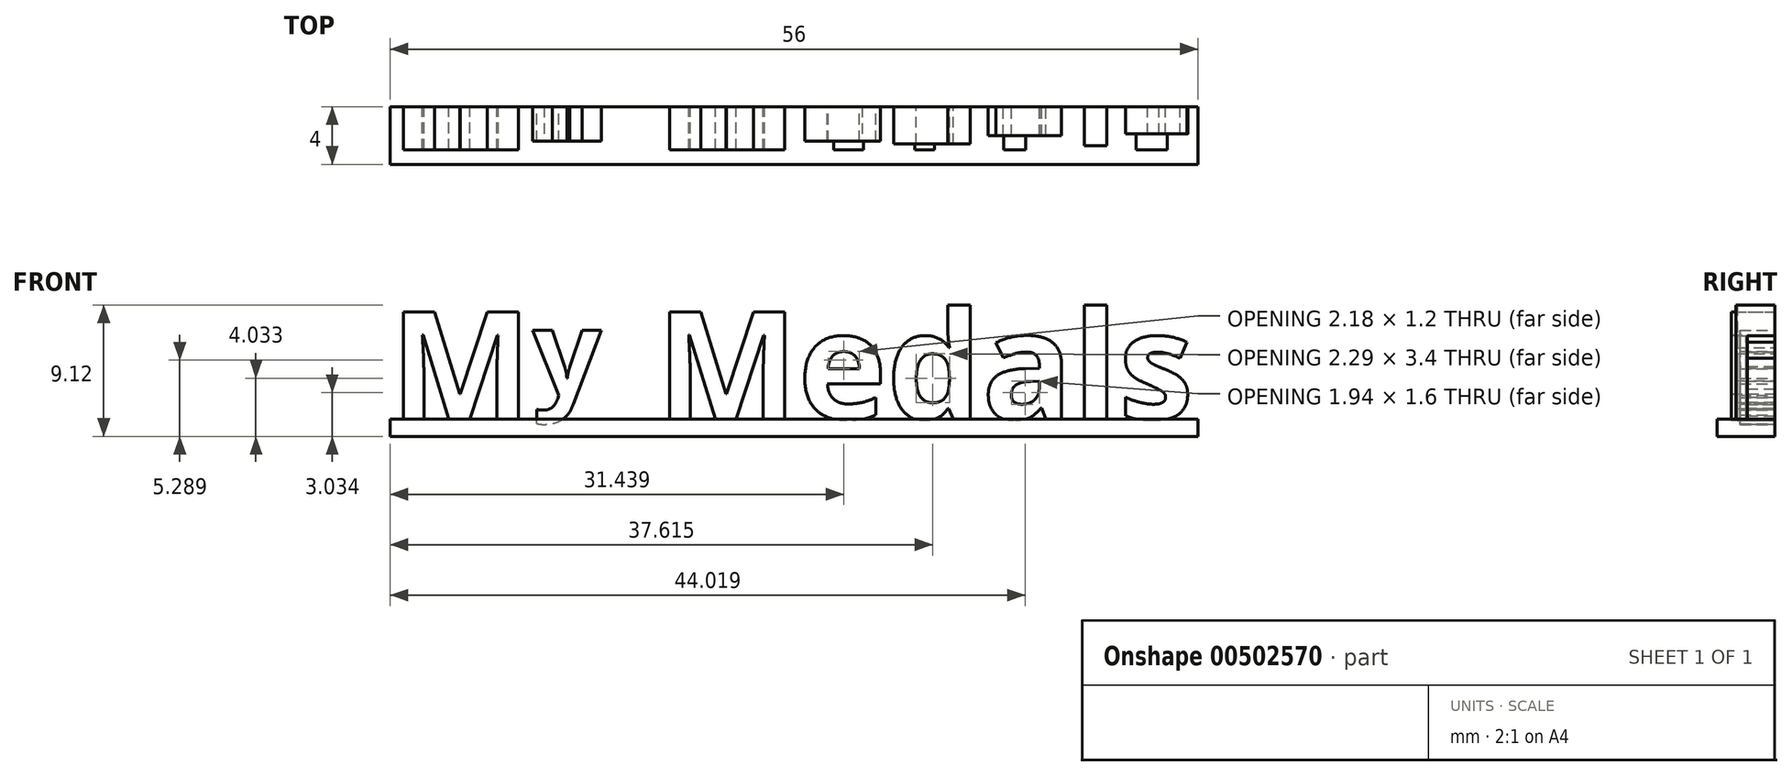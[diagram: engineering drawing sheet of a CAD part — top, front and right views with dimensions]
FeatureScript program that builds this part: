
annotation { "Feature Type Name" : "Feature", "Feature Type Description" : "" }
export const myFeature = defineFeature(function(context is Context, id is Id, definition is map)
    precondition{}
    {
        {
            var Q0;
            Q0=qCreatedBy(makeId("Front.planeOp"),FACE);
            var sketch = newSketch(context, id + "F0", { "sketchPlane" : qUnion([Q0])});
            skText(sketch, "E0", { "text": "My Medals", "fontName": "NotoSans-Bold.ttf"});
            const initialGuessF0  = {"E0": [0, 0, 1, 0, 0.0075]};
            skSetInitialGuess(sketch, initialGuessF0);
            skSolve(sketch);
        }
        {
            var Q0;
            Q0 = qSketchRegion(id + "F0", true);
            extrude(context, id + "F1", {"entities" : qUnion([Q0]), "depth" : 3 * mm, "offsetDistance" : 25 * mm});
        }
        {
            var Q0;
            Q0=makeQuery(id+"F1.opExtrude","SWEPT_BODY",BODY,{"disambiguationData":[OSD([sQuery(id+"F0.wireOp",EDGE,"E0.sketch_text.stroke-19"),sQuery(id+"F0.wireOp",EDGE,"E0.sketch_text.stroke-20"),sQuery(id+"F0.wireOp",EDGE,"E0.sketch_text.stroke-21"),sQuery(id+"F0.wireOp",EDGE,"E0.sketch_text.stroke-22"),sQuery(id+"F0.wireOp",EDGE,"E0.sketch_text.stroke-23"),sQuery(id+"F0.wireOp",EDGE,"E0.sketch_text.stroke-24"),sQuery(id+"F0.wireOp",EDGE,"E0.sketch_text.stroke-25"),sQuery(id+"F0.wireOp",EDGE,"E0.sketch_text.stroke-26"),sQuery(id+"F0.wireOp",EDGE,"E0.sketch_text.stroke-27"),sQuery(id+"F0.wireOp",EDGE,"E0.sketch_text.stroke-28"),sQuery(id+"F0.wireOp",EDGE,"E0.sketch_text.stroke-29"),sQuery(id+"F0.wireOp",EDGE,"E0.sketch_text.stroke-30"),sQuery(id+"F0.wireOp",EDGE,"E0.sketch_text.stroke-31"),sQuery(id+"F0.wireOp",EDGE,"E0.sketch_text.stroke-32"),sQuery(id+"F0.wireOp",EDGE,"E0.sketch_text.stroke-33"),sQuery(id+"F0.wireOp",EDGE,"E0.sketch_text.stroke-34"),sQuery(id+"F0.wireOp",EDGE,"E0.sketch_text.stroke-35")])]});
            transform(context, id + "F2", {"entities" : qUnion([Q0]), "transformType" : TransformType.TRANSLATION_3D, "dx" : 0 * mm, "dy" : 0 * mm, "dz" : 1.86 * mm, "makeCopy" : false});
        }
        {
            var Q0;
            Q0=qCreatedBy(makeId("Front.planeOp"),FACE);
            var sketch = newSketch(context, id + "F3", { "sketchPlane" : qUnion([Q0])});
            skLineSegment(sketch, "E1.bottom", {"start": v(19.37, -15.05) * mm, "end": v(75.37, -15.05) * mm});
            skLineSegment(sketch, "E1.top", {"start": v(19.37, -16.25) * mm, "end": v(75.37, -16.25) * mm});
            skLineSegment(sketch, "E1.left", {"start": v(19.37, -15.05) * mm, "end": v(19.37, -16.25) * mm});
            skLineSegment(sketch, "E1.right", {"start": v(75.37, -15.05) * mm, "end": v(75.37, -16.25) * mm});
            skSolve(sketch);
        }
        {
            var Q0;
            Q0=makeQuery(id+"F3.imprint","IMPRINT",FACE,{"disambiguationData":[TD([[makeQuery(id+"F3.imprint","IMPRINT",EDGE,{"derivedFrom":sQuery(id+"F3.wireOp",EDGE,"E1.bottom")}),-1.0]])]});
            extrude(context, id + "F4", {"entities" : qUnion([Q0]), "depth" : 4 * mm, "offsetDistance" : 25 * mm});
        }
        {
            var Q0;
            Q0=makeQuery(id+"F4.opExtrude","SWEPT_BODY",BODY,{"disambiguationData":[OSD([sQuery(id+"F3.wireOp",EDGE,"E1.bottom"),sQuery(id+"F3.wireOp",EDGE,"E1.top"),sQuery(id+"F3.wireOp",EDGE,"E1.left"),sQuery(id+"F3.wireOp",EDGE,"E1.right")])]});
            var Q1;
            Q1=makeQuery(id+"F4.opExtrude","CAP_VERTEX",VERTEX,{"disambiguationData":[OSD([sQuery(id+"F3.wireOp",EDGE,"E1.bottom"),sQuery(id+"F3.wireOp",EDGE,"E1.left")])],"isStart":true});
            var Q2;
            Q2=qCreatedBy(makeId("Origin.pointOp"),VERTEX);
            transform(context, id + "F5", {"entities" : qUnion([Q0]), "transformType" : TransformType.TRANSLATION_ENTITY, "oppositeDirectionEntity" : false, "transformLine" : qUnion([Q1, Q2]), "makeCopy" : false});
        }
        {
            var Q0;
            Q0=makeQuery(id+"F1.opExtrude","SWEPT_BODY",BODY,{"disambiguationData":[OSD([sQuery(id+"F0.wireOp",EDGE,"E0.sketch_text.stroke-19"),sQuery(id+"F0.wireOp",EDGE,"E0.sketch_text.stroke-20"),sQuery(id+"F0.wireOp",EDGE,"E0.sketch_text.stroke-21"),sQuery(id+"F0.wireOp",EDGE,"E0.sketch_text.stroke-22"),sQuery(id+"F0.wireOp",EDGE,"E0.sketch_text.stroke-23"),sQuery(id+"F0.wireOp",EDGE,"E0.sketch_text.stroke-24"),sQuery(id+"F0.wireOp",EDGE,"E0.sketch_text.stroke-25"),sQuery(id+"F0.wireOp",EDGE,"E0.sketch_text.stroke-26"),sQuery(id+"F0.wireOp",EDGE,"E0.sketch_text.stroke-27"),sQuery(id+"F0.wireOp",EDGE,"E0.sketch_text.stroke-28"),sQuery(id+"F0.wireOp",EDGE,"E0.sketch_text.stroke-29"),sQuery(id+"F0.wireOp",EDGE,"E0.sketch_text.stroke-30"),sQuery(id+"F0.wireOp",EDGE,"E0.sketch_text.stroke-31"),sQuery(id+"F0.wireOp",EDGE,"E0.sketch_text.stroke-32"),sQuery(id+"F0.wireOp",EDGE,"E0.sketch_text.stroke-33"),sQuery(id+"F0.wireOp",EDGE,"E0.sketch_text.stroke-34"),sQuery(id+"F0.wireOp",EDGE,"E0.sketch_text.stroke-35")])]});
            var Q1;
            Q1=makeQuery(id+"F1.opExtrude","CAP_VERTEX",VERTEX,{"disambiguationData":[OSD([sQuery(id+"F0.wireOp",EDGE,"E0.sketch_text.stroke-30"),sQuery(id+"F0.wireOp",EDGE,"E0.sketch_text.stroke-31")])],"isStart":true});
            transform(context, id + "F6", {"entities" : qUnion([Q0]), "transformType" : TransformType.SCALE_UNIFORMLY, "scale" : .8, "scalePoint" : qUnion([Q1]), "makeCopy" : false});
        }
        {
            var Q0;
            Q0=makeQuery(id+"F1.opExtrude","CAP_FACE",FACE,{"disambiguationData":[OSD([sQuery(id+"F0.wireOp",EDGE,"E0.sketch_text.stroke-55"),sQuery(id+"F0.wireOp",EDGE,"E0.sketch_text.stroke-56"),sQuery(id+"F0.wireOp",EDGE,"E0.sketch_text.stroke-57"),sQuery(id+"F0.wireOp",EDGE,"E0.sketch_text.stroke-58"),sQuery(id+"F0.wireOp",EDGE,"E0.sketch_text.stroke-59"),sQuery(id+"F0.wireOp",EDGE,"E0.sketch_text.stroke-60"),sQuery(id+"F0.wireOp",EDGE,"E0.sketch_text.stroke-61"),sQuery(id+"F0.wireOp",EDGE,"E0.sketch_text.stroke-62"),sQuery(id+"F0.wireOp",EDGE,"E0.sketch_text.stroke-63"),sQuery(id+"F0.wireOp",EDGE,"E0.sketch_text.stroke-64"),sQuery(id+"F0.wireOp",EDGE,"E0.sketch_text.stroke-65"),sQuery(id+"F0.wireOp",EDGE,"E0.sketch_text.stroke-66"),sQuery(id+"F0.wireOp",EDGE,"E0.sketch_text.stroke-67"),sQuery(id+"F0.wireOp",EDGE,"E0.sketch_text.stroke-68"),sQuery(id+"F0.wireOp",EDGE,"E0.sketch_text.stroke-69"),sQuery(id+"F0.wireOp",EDGE,"E0.sketch_text.stroke-70"),sQuery(id+"F0.wireOp",EDGE,"E0.sketch_text.stroke-71"),sQuery(id+"F0.wireOp",EDGE,"E0.sketch_text.stroke-72"),sQuery(id+"F0.wireOp",EDGE,"E0.sketch_text.stroke-73"),sQuery(id+"F0.wireOp",EDGE,"E0.sketch_text.stroke-74")])],"isStart":false});
            extrude(context, id + "F7", {"entities" : qUnion([Q0]), "operationType" : NewBodyOperationType.REMOVE, "oppositeDirection" : true, "depth" : .6 * mm, "offsetDistance" : 25 * mm});
        }
        {
            var Q0;
            Q0=makeQuery(id+"F1.opExtrude","CAP_FACE",FACE,{"disambiguationData":[OSD([sQuery(id+"F0.wireOp",EDGE,"E0.sketch_text.stroke-75"),sQuery(id+"F0.wireOp",EDGE,"E0.sketch_text.stroke-76"),sQuery(id+"F0.wireOp",EDGE,"E0.sketch_text.stroke-77"),sQuery(id+"F0.wireOp",EDGE,"E0.sketch_text.stroke-78"),sQuery(id+"F0.wireOp",EDGE,"E0.sketch_text.stroke-79"),sQuery(id+"F0.wireOp",EDGE,"E0.sketch_text.stroke-80"),sQuery(id+"F0.wireOp",EDGE,"E0.sketch_text.stroke-81"),sQuery(id+"F0.wireOp",EDGE,"E0.sketch_text.stroke-82"),sQuery(id+"F0.wireOp",EDGE,"E0.sketch_text.stroke-83"),sQuery(id+"F0.wireOp",EDGE,"E0.sketch_text.stroke-84"),sQuery(id+"F0.wireOp",EDGE,"E0.sketch_text.stroke-85"),sQuery(id+"F0.wireOp",EDGE,"E0.sketch_text.stroke-86"),sQuery(id+"F0.wireOp",EDGE,"E0.sketch_text.stroke-87"),sQuery(id+"F0.wireOp",EDGE,"E0.sketch_text.stroke-88"),sQuery(id+"F0.wireOp",EDGE,"E0.sketch_text.stroke-89"),sQuery(id+"F0.wireOp",EDGE,"E0.sketch_text.stroke-90"),sQuery(id+"F0.wireOp",EDGE,"E0.sketch_text.stroke-91"),sQuery(id+"F0.wireOp",EDGE,"E0.sketch_text.stroke-92"),sQuery(id+"F0.wireOp",EDGE,"E0.sketch_text.stroke-93"),sQuery(id+"F0.wireOp",EDGE,"E0.sketch_text.stroke-94"),sQuery(id+"F0.wireOp",EDGE,"E0.sketch_text.stroke-95"),sQuery(id+"F0.wireOp",EDGE,"E0.sketch_text.stroke-96"),sQuery(id+"F0.wireOp",EDGE,"E0.sketch_text.stroke-97")])],"isStart":false});
            extrude(context, id + "F8", {"entities" : qUnion([Q0]), "operationType" : NewBodyOperationType.REMOVE, "oppositeDirection" : true, "depth" : .4 * mm, "offsetDistance" : 25 * mm});
        }
        {
            var Q0;
            Q0=makeQuery(id+"F1.opExtrude","CAP_FACE",FACE,{"disambiguationData":[OSD([sQuery(id+"F0.wireOp",EDGE,"E0.sketch_text.stroke-98"),sQuery(id+"F0.wireOp",EDGE,"E0.sketch_text.stroke-99"),sQuery(id+"F0.wireOp",EDGE,"E0.sketch_text.stroke-100"),sQuery(id+"F0.wireOp",EDGE,"E0.sketch_text.stroke-101"),sQuery(id+"F0.wireOp",EDGE,"E0.sketch_text.stroke-102"),sQuery(id+"F0.wireOp",EDGE,"E0.sketch_text.stroke-103"),sQuery(id+"F0.wireOp",EDGE,"E0.sketch_text.stroke-104"),sQuery(id+"F0.wireOp",EDGE,"E0.sketch_text.stroke-105"),sQuery(id+"F0.wireOp",EDGE,"E0.sketch_text.stroke-106"),sQuery(id+"F0.wireOp",EDGE,"E0.sketch_text.stroke-107"),sQuery(id+"F0.wireOp",EDGE,"E0.sketch_text.stroke-108"),sQuery(id+"F0.wireOp",EDGE,"E0.sketch_text.stroke-109"),sQuery(id+"F0.wireOp",EDGE,"E0.sketch_text.stroke-110"),sQuery(id+"F0.wireOp",EDGE,"E0.sketch_text.stroke-111"),sQuery(id+"F0.wireOp",EDGE,"E0.sketch_text.stroke-112"),sQuery(id+"F0.wireOp",EDGE,"E0.sketch_text.stroke-113"),sQuery(id+"F0.wireOp",EDGE,"E0.sketch_text.stroke-114"),sQuery(id+"F0.wireOp",EDGE,"E0.sketch_text.stroke-115"),sQuery(id+"F0.wireOp",EDGE,"E0.sketch_text.stroke-116"),sQuery(id+"F0.wireOp",EDGE,"E0.sketch_text.stroke-117"),sQuery(id+"F0.wireOp",EDGE,"E0.sketch_text.stroke-118"),sQuery(id+"F0.wireOp",EDGE,"E0.sketch_text.stroke-119"),sQuery(id+"F0.wireOp",EDGE,"E0.sketch_text.stroke-120"),sQuery(id+"F0.wireOp",EDGE,"E0.sketch_text.stroke-121"),sQuery(id+"F0.wireOp",EDGE,"E0.sketch_text.stroke-122")])],"isStart":false});
            extrude(context, id + "F9", {"entities" : qUnion([Q0]), "operationType" : NewBodyOperationType.REMOVE, "oppositeDirection" : true, "depth" : 1 * mm, "offsetDistance" : 25 * mm});
        }
        {
            var Q0;
            Q0=makeQuery(id+"F1.opExtrude","CAP_FACE",FACE,{"disambiguationData":[OSD([sQuery(id+"F0.wireOp",EDGE,"E0.sketch_text.stroke-123"),sQuery(id+"F0.wireOp",EDGE,"E0.sketch_text.stroke-124"),sQuery(id+"F0.wireOp",EDGE,"E0.sketch_text.stroke-125"),sQuery(id+"F0.wireOp",EDGE,"E0.sketch_text.stroke-126")])],"isStart":false});
            extrude(context, id + "F10", {"entities" : qUnion([Q0]), "operationType" : NewBodyOperationType.REMOVE, "oppositeDirection" : true, "depth" : .3 * mm, "offsetDistance" : 25 * mm});
        }
        {
            var Q0;
            Q0=makeQuery(id+"F1.opExtrude","CAP_FACE",FACE,{"disambiguationData":[OSD([sQuery(id+"F0.wireOp",EDGE,"E0.sketch_text.stroke-127"),sQuery(id+"F0.wireOp",EDGE,"E0.sketch_text.stroke-128"),sQuery(id+"F0.wireOp",EDGE,"E0.sketch_text.stroke-129"),sQuery(id+"F0.wireOp",EDGE,"E0.sketch_text.stroke-130"),sQuery(id+"F0.wireOp",EDGE,"E0.sketch_text.stroke-131"),sQuery(id+"F0.wireOp",EDGE,"E0.sketch_text.stroke-132"),sQuery(id+"F0.wireOp",EDGE,"E0.sketch_text.stroke-133"),sQuery(id+"F0.wireOp",EDGE,"E0.sketch_text.stroke-134"),sQuery(id+"F0.wireOp",EDGE,"E0.sketch_text.stroke-135"),sQuery(id+"F0.wireOp",EDGE,"E0.sketch_text.stroke-136"),sQuery(id+"F0.wireOp",EDGE,"E0.sketch_text.stroke-137"),sQuery(id+"F0.wireOp",EDGE,"E0.sketch_text.stroke-138"),sQuery(id+"F0.wireOp",EDGE,"E0.sketch_text.stroke-139"),sQuery(id+"F0.wireOp",EDGE,"E0.sketch_text.stroke-140"),sQuery(id+"F0.wireOp",EDGE,"E0.sketch_text.stroke-141"),sQuery(id+"F0.wireOp",EDGE,"E0.sketch_text.stroke-142"),sQuery(id+"F0.wireOp",EDGE,"E0.sketch_text.stroke-143"),sQuery(id+"F0.wireOp",EDGE,"E0.sketch_text.stroke-144"),sQuery(id+"F0.wireOp",EDGE,"E0.sketch_text.stroke-145"),sQuery(id+"F0.wireOp",EDGE,"E0.sketch_text.stroke-146"),sQuery(id+"F0.wireOp",EDGE,"E0.sketch_text.stroke-147"),sQuery(id+"F0.wireOp",EDGE,"E0.sketch_text.stroke-148"),sQuery(id+"F0.wireOp",EDGE,"E0.sketch_text.stroke-149"),sQuery(id+"F0.wireOp",EDGE,"E0.sketch_text.stroke-150"),sQuery(id+"F0.wireOp",EDGE,"E0.sketch_text.stroke-151"),sQuery(id+"F0.wireOp",EDGE,"E0.sketch_text.stroke-152")])],"isStart":false});
            extrude(context, id + "F11", {"entities" : qUnion([Q0]), "operationType" : NewBodyOperationType.REMOVE, "oppositeDirection" : true, "depth" : 1.1 * mm, "offsetDistance" : 25 * mm});
        }
    });
